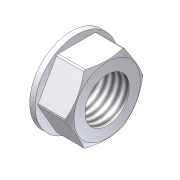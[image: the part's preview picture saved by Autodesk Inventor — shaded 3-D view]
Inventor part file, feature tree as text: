
AUTODESK INVENTOR PART (.ipt)
format: ipt  version: unknown  size: 210,432 bytes
history: native  units: in
note: dims shown in document units (in); Inventor stores cm internally (conversion verified against a paired STEP export)
features: sketch x4, extrude x3, chamfer x2, revolve x1, thread x1
ambient origin geometry x8: Origin, YZ Plane, XZ Plane, XY Plane, X Axis, Y Axis, Z Axis, Center Point
feature tree (11):
  revolve  "Revolution3"  [1 undecoded]
  chamfer  "Chamfer2"  Distance=0.0394in Angle=30.0deg
  chamfer  "Chamfer3"  Distance=0.2795in
  extrude  "Extrusion15"  Depth=0.3937in TaperAngle=0.0deg
  extrude  "Extrusion16"  Depth=0.0394in TaperAngle=30.0deg
  extrude  "Extrusion17"  Depth=0.0591in TaperAngle=0.0deg
  thread  "Thread2"  [1 undecoded]
  sketch  "Sketch17"  dims[d96=0.1575in d98=0.2756in]
  sketch  "Sketch18"  dims[d99=0.0in]
  sketch  "Sketch19"  dims[d100=0.2756in]
  sketch  "Sketch20"  dims[d102=90.0deg d103=0.0394in d104=0.0787in d105=30.0deg d106=0.2795in d107=0.3937in d108=0.0in d109=0.0394in d110=0.0787in d111=30.0deg d112=0.0591in d113=0.0in d114=0.5906in d115=0.0197in d116=0.0in d117=0.3937in d118=0.0in]
note: 2 required parameter values undecoded (feature->parameter linkage not recoverable at this tier; creation-order binding heuristic only, values carry confidence <= 0.55)